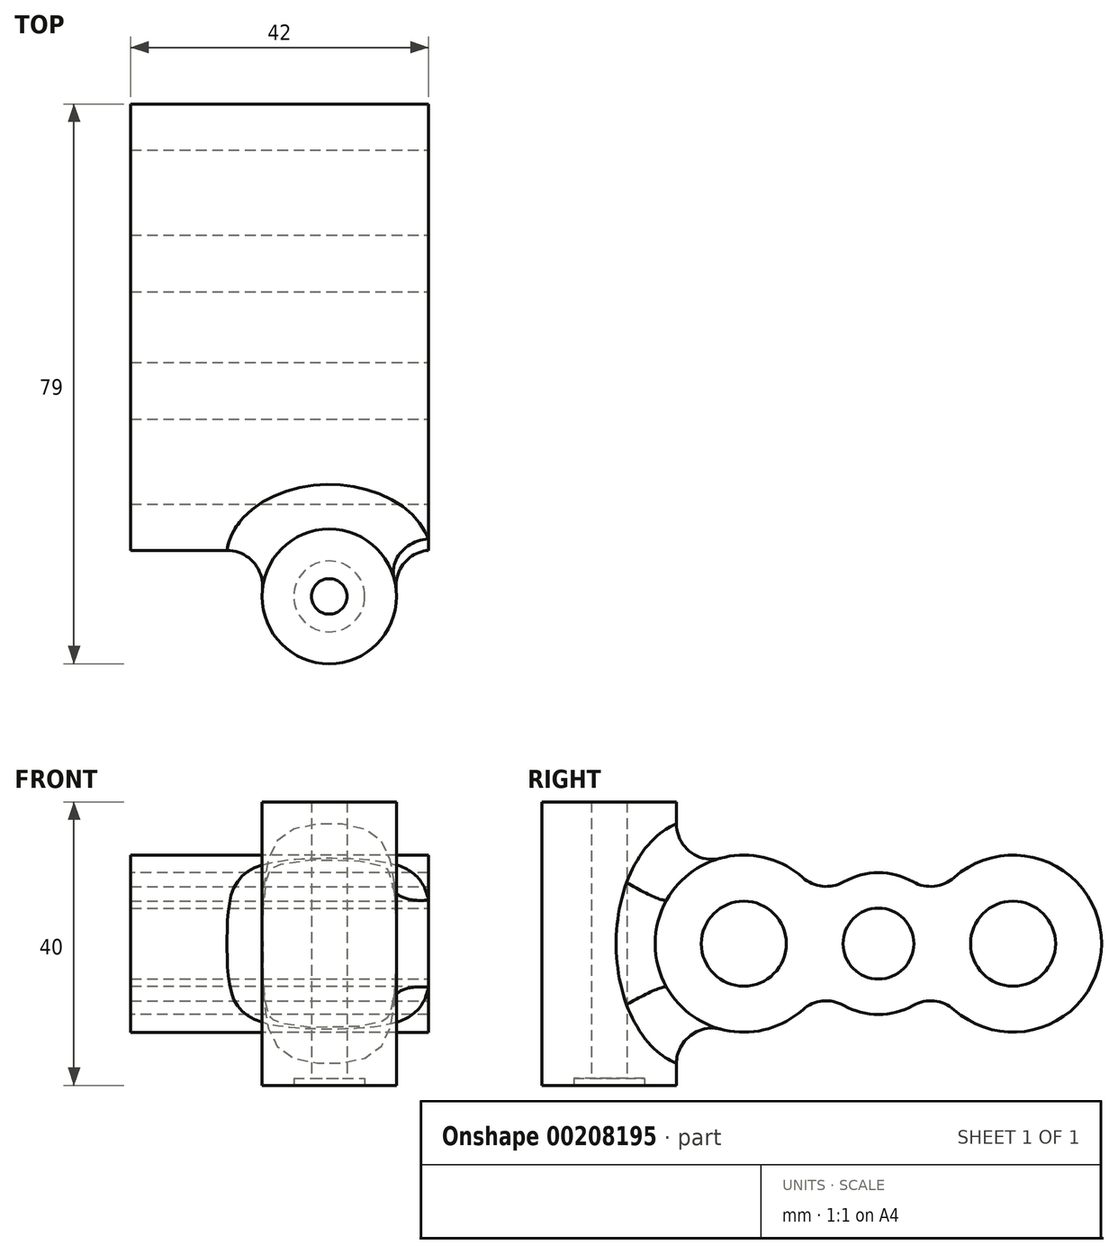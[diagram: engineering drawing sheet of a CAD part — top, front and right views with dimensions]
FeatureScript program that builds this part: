
annotation { "Feature Type Name" : "Feature", "Feature Type Description" : "" }
export const myFeature = defineFeature(function(context is Context, id is Id, definition is map)
    precondition{}
    {
        {
            var Q0;
            Q0=qCreatedBy(makeId("Right.planeOp"),FACE);
            var sketch = newSketch(context, id + "F0", { "sketchPlane" : qUnion([Q0])});
            skArc(sketch, "E0", {"start": v(-8.02, 5.97) * mm, "mid": v(-31.5, 0) * mm, "end": v(-8.02, -5.97) * mm});
            skArc(sketch, "E1", {"start": v(-8.02, -5.97) * mm, "mid": v(0, -10) * mm, "end": v(8.02, -5.97) * mm});
            skArc(sketch, "E2", {"start": v(8.02, -5.97) * mm, "mid": v(31.5, 0) * mm, "end": v(8.02, 5.97) * mm});
            skArc(sketch, "E3.trimOffspring", {"start": v(8.02, 5.97) * mm, "mid": v(0, 10) * mm, "end": v(-8.02, 5.97) * mm});
            skSolve(sketch);
        }
        {
            var Q0;
            Q0 = qSketchRegion(id + "F0", true);
            var Q1;
            {var subQ0=sQuery(id+"F0.wireOp",EDGE,"E1");var subQ1=sQuery(id+"F0.wireOp",EDGE,"E0");var subQ2=makeQuery(id+"F0.imprint","INTERSECT",VERTEX,{"disambiguationData":[OD(0.0)],"derivedFrom":[subQ1,subQ0]});Q1=makeQuery(id+"F0.imprint","IMPRINT",FACE,{"disambiguationData":[TD([[makeQuery(id+"F0.imprint","IMPRINT",EDGE,{"disambiguationData":[TD([[subQ2,-1.0]])],"derivedFrom":subQ1}),1.0]])]});}
            extrude(context, id + "F1", {"entities" : qUnion([Q0, Q1]), "depth" : 42 * mm});
        }
        {
            var Q0;
            Q0=makeQuery(id+"F1.opExtrude","CAP_FACE",FACE,{"disambiguationData":[OSD([sQuery(id+"F0.wireOp",EDGE,"E0"),sQuery(id+"F0.wireOp",EDGE,"E1"),sQuery(id+"F0.wireOp",EDGE,"E2")])],"isStart":false});
            var sketch = newSketch(context, id + "F2", { "sketchPlane" : qUnion([Q0])});
            skCircle(sketch, "E4", {"center": v(-19, 0) * mm, "radius": 6 * mm});
            skCircle(sketch, "E5", {"center": v(0, 0) * mm, "radius": 5 * mm});
            skCircle(sketch, "E6", {"center": v(19, 0) * mm, "radius": 6 * mm});
            skSolve(sketch);
        }
        {
            var Q0;
            Q0=makeQuery(id+"F2.imprint","IMPRINT",FACE,{"disambiguationData":[TD([[makeQuery(id+"F2.imprint","IMPRINT",EDGE,{"derivedFrom":sQuery(id+"F2.wireOp",EDGE,"E5")}),1.0]])]});
            var Q1;
            Q1=makeQuery(id+"F2.imprint","IMPRINT",FACE,{"disambiguationData":[TD([[makeQuery(id+"F2.imprint","IMPRINT",EDGE,{"derivedFrom":sQuery(id+"F2.wireOp",EDGE,"E6")}),1.0]])]});
            var Q2;
            Q2=makeQuery(id+"F2.imprint","IMPRINT",FACE,{"disambiguationData":[TD([[makeQuery(id+"F2.imprint","IMPRINT",EDGE,{"derivedFrom":sQuery(id+"F2.wireOp",EDGE,"E4")}),1.0]])]});
            extrude(context, id + "F3", {"entities" : qUnion([Q0, Q1, Q2]), "operationType" : NewBodyOperationType.REMOVE, "endBound" : BoundingType.THROUGH_ALL, "oppositeDirection" : true, "depth" : 25 * mm});
        }
        {
            var Q0;
            Q0=qCreatedBy(makeId("Top.planeOp"),FACE);
            var sketch = newSketch(context, id + "F4", { "sketchPlane" : qUnion([Q0])});
            skCircle(sketch, "E7", {"center": v(28, -38) * mm, "radius": 9.5 * mm});
            skSolve(sketch);
        }
        {
            var Q0;
            Q0 = qSketchRegion(id + "F4", true);
            extrude(context, id + "F5", {"entities" : qUnion([Q0]), "operationType" : NewBodyOperationType.ADD, "endBound" : BoundingType.SYMMETRIC, "depth" : 40 * mm});
        }
        {
            var Q0;
            Q0=makeQuery(id+"F5.opExtrude","CAP_FACE",FACE,{"disambiguationData":[OSD([sQuery(id+"F4.wireOp",EDGE,"E7")])],"isStart":true});
            var sketch = newSketch(context, id + "F6", { "sketchPlane" : qUnion([Q0])});
            skPoint(sketch, "E8", {"position": v(28, 38) * mm});
            skSolve(sketch);
        }
        {
            var Q0;
            Q0=sQuery(id+"F6.wireOp",VERTEX,"E8");
            var Q1;
            Q1=makeQuery(id+"F1.opExtrude","SWEPT_BODY",BODY,{"disambiguationData":[OSD([sQuery(id+"F0.wireOp",EDGE,"E0"),sQuery(id+"F0.wireOp",EDGE,"E1"),sQuery(id+"F0.wireOp",EDGE,"E2"),sQuery(id+"F0.wireOp",EDGE,"E3.trimOffspring")])]});
            hole(context, id + "F7", {"style" : HoleStyle.C_BORE, "endStyle" : HoleEndStyle.THROUGH, "holeDiameter" : 5 * mm, "cBoreDiameter" : 10 * mm, "cBoreDepth" : mm, "locations" : qUnion([Q0]), "scope" : qUnion([Q1]), "isTappedThrough" : true});
        }
        {
            var Q0;
            Q0=makeQuery(id+"F5.boolean.opBoolean","INTERSECT",EDGE,{"derivedFrom":[makeQuery(id+"F1.opExtrude","SWEPT_FACE",FACE,{"disambiguationData":[OSD([sQuery(id+"F0.wireOp",EDGE,"E0")])]}),makeQuery(id+"F5.opExtrude","SWEPT_FACE",FACE,{"disambiguationData":[OSD([sQuery(id+"F4.wireOp",EDGE,"E7")])]})]});
            fillet(context, id + "F8", {"entities" : qUnion([Q0]), "radius" : 5 * mm, "tangentPropagation" : true, "allowEdgeOverflow" : false});
        }
        {
            var Q0;
            Q0=makeQuery(id+"F1.opExtrude","SWEPT_EDGE",EDGE,{"disambiguationData":[OSD([sQuery(id+"F0.wireOp",EDGE,"E0"),sQuery(id+"F0.wireOp",EDGE,"E1")])]});
            var Q1;
            Q1=makeQuery(id+"F1.opExtrude","SWEPT_EDGE",EDGE,{"disambiguationData":[OSD([sQuery(id+"F0.wireOp",EDGE,"E1"),sQuery(id+"F0.wireOp",EDGE,"E2")])]});
            var Q2;
            Q2=makeQuery(id+"F1.opExtrude","SWEPT_EDGE",EDGE,{"disambiguationData":[OSD([sQuery(id+"F0.wireOp",EDGE,"E0"),sQuery(id+"F0.wireOp",EDGE,"E3.trimOffspring")])]});
            var Q3;
            Q3=makeQuery(id+"F1.opExtrude","SWEPT_EDGE",EDGE,{"disambiguationData":[OSD([sQuery(id+"F0.wireOp",EDGE,"E2"),sQuery(id+"F0.wireOp",EDGE,"E3.trimOffspring")])]});
            fillet(context, id + "F9", {"entities" : qUnion([Q0, Q1, Q2, Q3]), "radius" : 5 * mm, "tangentPropagation" : true, "allowEdgeOverflow" : false});
        }
    });
